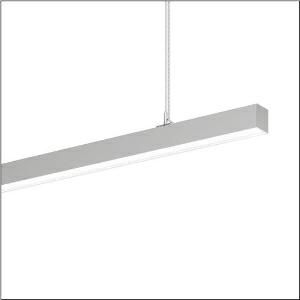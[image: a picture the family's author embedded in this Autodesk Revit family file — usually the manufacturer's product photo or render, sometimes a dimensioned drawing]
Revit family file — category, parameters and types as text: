
# Revit family: silica_r__21_51mx30tbt5s_71cb
name_source: partatom
category: Lighting Fixtures
units: mm (PartAtom-declared; Revit-internal decimal feet)

## family parameters
Cut with Voids When Loaded = No
Host = Face
Light Source = No
Part Type = Normal
Room Calculation Point = No
Round Connector Dimension = Use Diameter
Shared = No

## types (1)
- --- (1 x LED, 5150 lm, 42.2 W, 6500K)
    Apparent Load = 42 VA
    CIE Flux Codes = 47 79 96 58 100
    Color Rendering = 80
    Color Temperature = 6500K
    Default Elevation = 1800 mm
    Description = Silica® 21, office luminaire, primary optical cover: cover, of PMMA, opal, light emission: direct/indirect distribution, primary light characteristic: symmetric, installation type: suspended mounting, LED, rated luminous flux: 5.150lm, luminous efficacy: 116lm/W, light colour: 8tw, colour temperature: 2700..6500K, control gear: ECG DALI, with terminal, 3+2-pole, max. 2.5mm², mains connection: 220..240V, AC, 50/60Hz, rated input power: 44.3W, luminaire housing, of aluminium, metallic grey (RAL 9006), length: 1.504mm, width: 53mm, height: 53mm, protection rating (complete): IP20, insulation class (complete): insulation class I (protective earthing), certification: CE, permissible operating ambient temperature: 0..+35°C, standard: EN 50419, packaging unit: 1 piece
    Height = 53 mm
    Lamp = 1 x LED
    Lamp Light Flux = 5150 lm
    Lamp Power = 42.2 W
    Lamp count = 1
    Length = 1504 mm
    Luminous efficacy = 122 lm/W
    Manufacturer = Siteco
    ModVariant = No
    Model = 51MX30TBT5S
    Mounting Place = Ceiling
    Mounting Type = Pendant
    Number of Poles = 1
    OnlyDefault = Yes
    Power Factor = 1
    Product Name = Silica® 21
    Product group = office luminaire | ceiling pendant
    ProductGroupID = 902
    Protection Class = Protection class I
    Protection Degree = IP 20
    RLX_Detail_Level = 1
    RLX_Emergency_Light_Flux = 0 lm
    RLX_Emergency_Type = 0
    RLX_Emergency_Type_DB = No
    RlxData = <blob elided: 20177 chars, md5=8c937725>
    Socket = socket
    Standby Power = 0 W
    System Light Flux = 5150 lm
    System Power = 42 W
    Type Comments = individual setting
    Type Image = l_1335864.jpg
    URL = http://relux.com
    VarID = @adj_109417
    Voltage = 0 V
    Weight = 0.00 kg
    Width = 53 mm

## geometry (parser evidence)
native form markers: Blend x4, Sweep x12
no freeform markers — native parametric forms only
